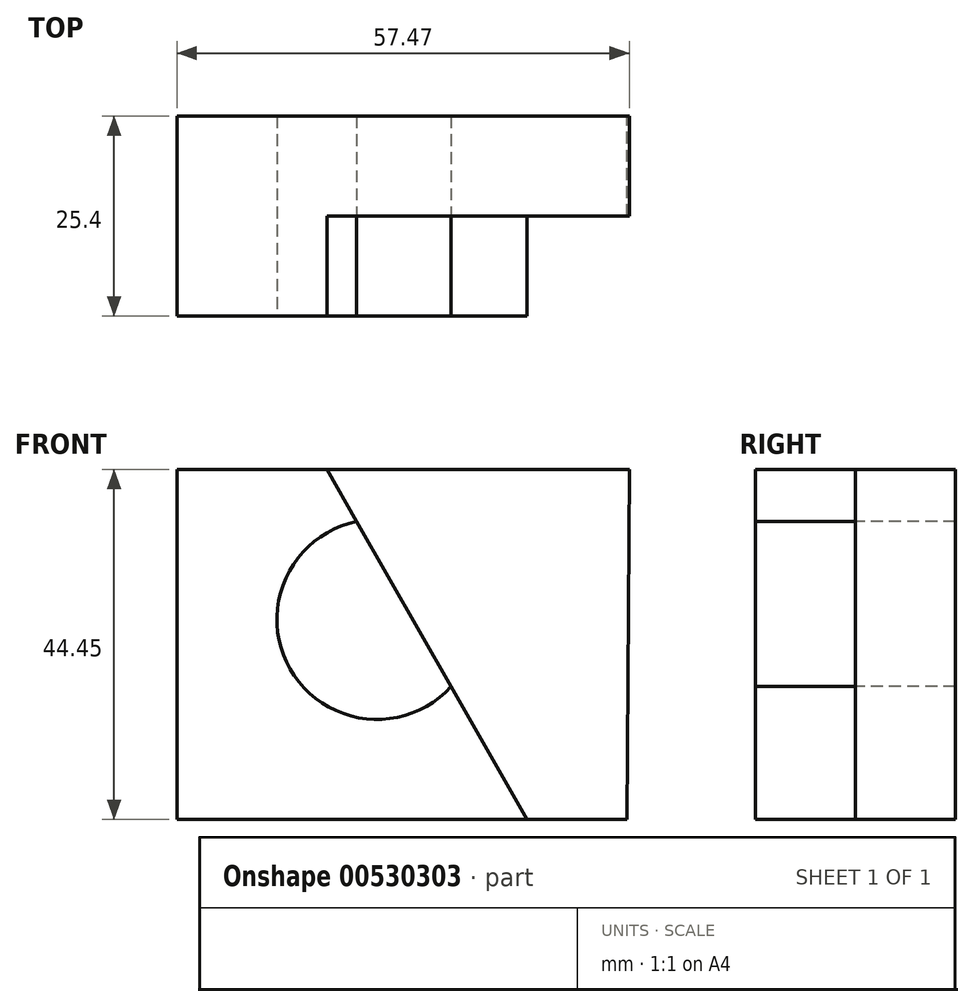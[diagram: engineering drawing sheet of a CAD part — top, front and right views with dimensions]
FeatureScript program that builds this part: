
annotation { "Feature Type Name" : "Feature", "Feature Type Description" : "" }
export const myFeature = defineFeature(function(context is Context, id is Id, definition is map)
    precondition{}
    {
        {
            var Q0;
            Q0=qCreatedBy(makeId("Front.planeOp"),FACE);
            var sketch = newSketch(context, id + "F0", { "sketchPlane" : qUnion([Q0])});
            skLineSegment(sketch, "E0", {"start": v(-28.24, 34.02) * mm, "end": v(-28.24, -10.43) * mm});
            skLineSegment(sketch, "E1", {"start": v(-28.24, -10.43) * mm, "end": v(28.91, -10.43) * mm});
            skLineSegment(sketch, "E2", {"start": v(29.23, 34.02) * mm, "end": v(-28.24, 34.02) * mm});
            skLineSegment(sketch, "E3", {"start": v(28.91, -10.43) * mm, "end": v(29.23, 34.02) * mm});
            skSolve(sketch);
        }
        {
            var Q0;
            Q0=makeQuery(id+"F0.imprint","IMPRINT",FACE,{"disambiguationData":[TD([[makeQuery(id+"F0.imprint","IMPRINT",EDGE,{"derivedFrom":sQuery(id+"F0.wireOp",EDGE,"E0")}),1.0]])]});
            extrude(context, id + "F1", {"entities" : qUnion([Q0]), "depth" : 25.4 * mm, "offsetDistance" : 25.4 * mm});
        }
        {
            var Q0;
            Q0=makeQuery(id+"F1.opExtrude","CAP_FACE",FACE,{"disambiguationData":[OSD([sQuery(id+"F0.wireOp",EDGE,"E0"),sQuery(id+"F0.wireOp",EDGE,"E1"),sQuery(id+"F0.wireOp",EDGE,"E2"),sQuery(id+"F0.wireOp",EDGE,"E3")])],"isStart":false});
            var sketch = newSketch(context, id + "F2", { "sketchPlane" : qUnion([Q0])});
            skLineSegment(sketch, "E4", {"start": v(-9.19, 34.02) * mm, "end": v(16.21, -10.43) * mm});
            skLineSegment(sketch, "E5", {"start": v(-9.19, 34.02) * mm, "end": v(-28.24, 34.02) * mm});
            skLineSegment(sketch, "E6", {"start": v(16.21, -10.43) * mm, "end": v(28.91, -10.43) * mm});
            skSolve(sketch);
        }
        {
            var Q0;
            {var subQ0=sQuery(id+"F2.wireOp",EDGE,"E4");Q0=makeQuery(id+"F2.imprint","IMPRINT",FACE,{"disambiguationData":[TD([[makeQuery(id+"F2.imprint","IMPRINT",EDGE,{"derivedFrom":subQ0}),1.0]])]});}
            extrude(context, id + "F3", {"entities" : qUnion([Q0]), "operationType" : NewBodyOperationType.REMOVE, "oppositeDirection" : true, "depth" : 12.7 * mm, "offsetDistance" : 25.4 * mm});
        }
        {
            var Q0;
            Q0=makeQuery(id+"F1.opExtrude","CAP_FACE",FACE,{"disambiguationData":[OSD([sQuery(id+"F0.wireOp",EDGE,"E0"),sQuery(id+"F0.wireOp",EDGE,"E1"),sQuery(id+"F0.wireOp",EDGE,"E2"),sQuery(id+"F0.wireOp",EDGE,"E3")])],"isStart":false});
            var sketch = newSketch(context, id + "F4", { "sketchPlane" : qUnion([Q0])});
            skCircle(sketch, "E7", {"center": v(-2.84, 14.97) * mm, "radius": 12.7 * mm});
            skLineSegment(sketch, "E8", {"start": v(-2.84, 14.97) * mm, "end": v(-2.84, -10.43) * mm});
            skLineSegment(sketch, "E9", {"start": v(-2.84, 14.97) * mm, "end": v(-28.24, 14.97) * mm});
            skSolve(sketch);
        }
        {
            var Q0;
            {var subQ0=sQuery(id+"F4.wireOp",EDGE,"E9");var subQ3=sQuery(id+"F4.wireOp",EDGE,"E7");var subQ4=makeQuery(id+"F4.imprint","INTERSECT",VERTEX,{"derivedFrom":[subQ3,subQ0]});Q0=makeQuery(id+"F4.imprint","IMPRINT",FACE,{"disambiguationData":[TD([[makeQuery(id+"F4.imprint","IMPRINT",EDGE,{"disambiguationData":[TD([[subQ4,1.0]])],"derivedFrom":subQ3}),1.0]])]});}
            var Q1;
            {var subQ0=sQuery(id+"F4.wireOp",EDGE,"E9");var subQ1=sQuery(id+"F4.wireOp",EDGE,"E7");var subQ2=makeQuery(id+"F4.imprint","INTERSECT",VERTEX,{"derivedFrom":[subQ1,subQ0]});Q1=makeQuery(id+"F4.imprint","IMPRINT",FACE,{"disambiguationData":[TD([[makeQuery(id+"F4.imprint","IMPRINT",EDGE,{"disambiguationData":[TD([[subQ2,-1.0]])],"derivedFrom":subQ1}),1.0]])]});}
            var Q2;
            {var subQ0=sQuery(id+"F4.wireOp",EDGE,"E7");var subQ1=makeQuery(id+"F3.boolean.opBoolean","COPY",EDGE,{"derivedFrom":makeQuery(id+"F3.opExtrude","CAP_EDGE",EDGE,{"disambiguationData":[OSD([sQuery(id+"F2.wireOp",EDGE,"E4")])],"isStart":true})});var subQ2=makeQuery(id+"F4.imprint","INTERSECT",VERTEX,{"disambiguationData":[OD(0.0)],"derivedFrom":[subQ1,subQ0]});Q2=makeQuery(id+"F4.imprint","IMPRINT",FACE,{"disambiguationData":[TD([[makeQuery(id+"F4.imprint","IMPRINT",EDGE,{"disambiguationData":[TD([[subQ2,1.0]])],"derivedFrom":subQ0}),1.0]])]});}
            extrude(context, id + "F5", {"entities" : qUnion([Q0, Q1, Q2]), "operationType" : NewBodyOperationType.REMOVE, "endBound" : BoundingType.THROUGH_ALL, "oppositeDirection" : true, "depth" : 25.4 * mm, "offsetDistance" : 25.4 * mm});
        }
    });
